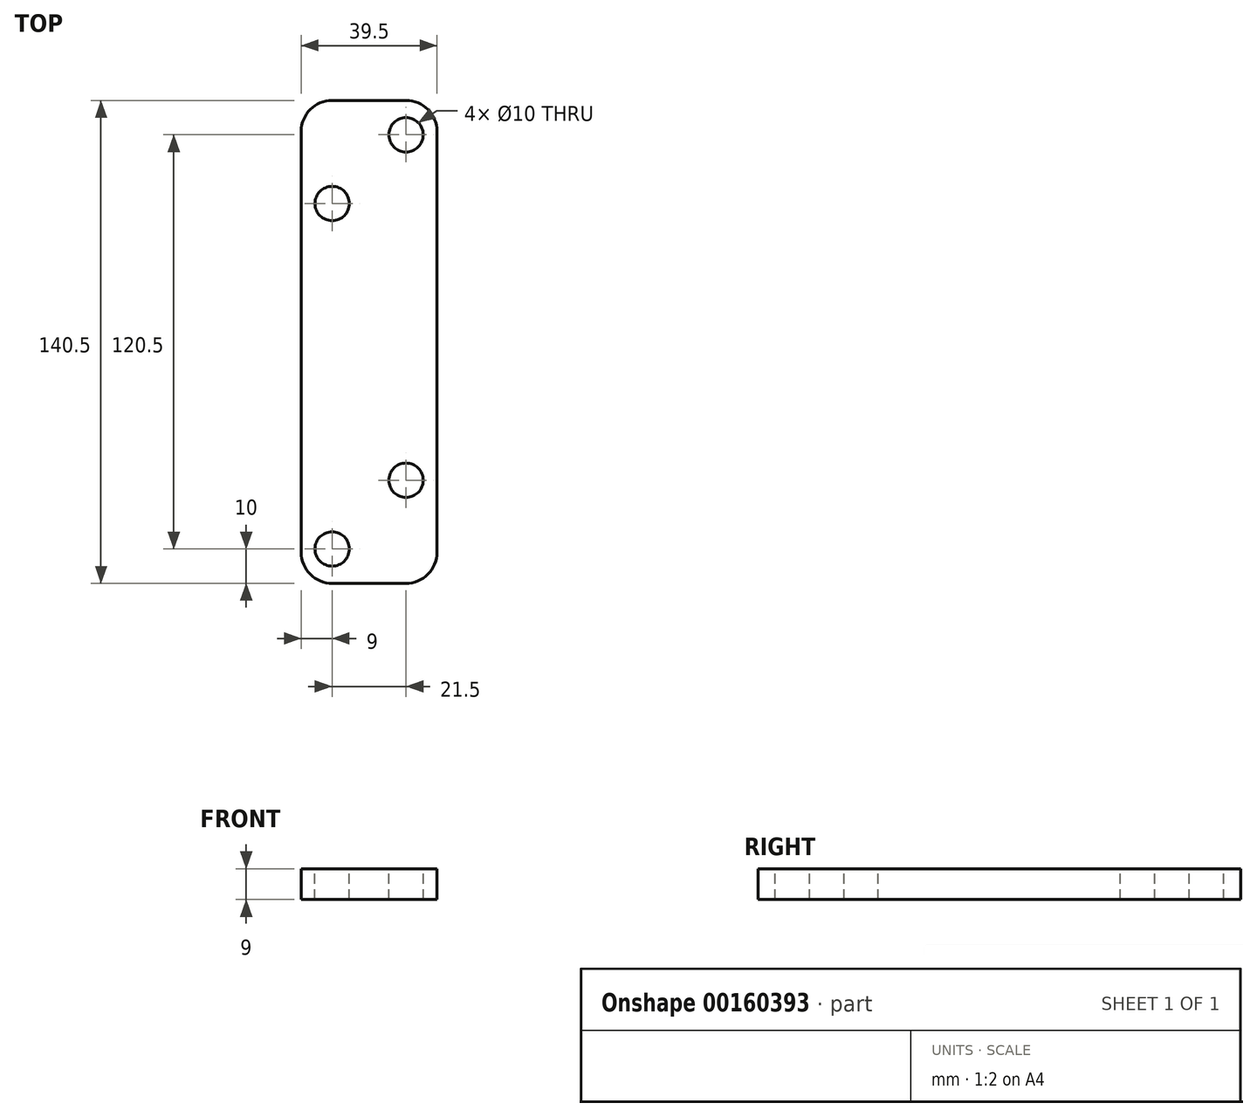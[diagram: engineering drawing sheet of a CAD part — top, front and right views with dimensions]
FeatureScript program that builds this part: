
annotation { "Feature Type Name" : "Feature", "Feature Type Description" : "" }
export const myFeature = defineFeature(function(context is Context, id is Id, definition is map)
    precondition{}
    {
        {
            var Q0;
            Q0=qCreatedBy(makeId("Top.planeOp"),FACE);
            var sketch = newSketch(context, id + "F0", { "sketchPlane" : qUnion([Q0])});
            skLineSegment(sketch, "E0.bottom", {"start": v(-10.75, 65.25) * mm, "end": v(10.75, 65.25) * mm, "construction": true});
            skLineSegment(sketch, "E0.top", {"start": v(-10.75, -65.25) * mm, "end": v(10.75, -65.25) * mm, "construction": true});
            skLineSegment(sketch, "E0.left", {"start": v(-14.75, 61.25) * mm, "end": v(-14.75, -61.25) * mm, "construction": true});
            skLineSegment(sketch, "E0.right", {"start": v(14.75, 61.25) * mm, "end": v(14.75, -61.25) * mm, "construction": true});
            skPoint(sketch, "E0.middle", {"position": v(0, 0) * mm});
            skPoint(sketch, "E1.visualSharp", {"position": v(-14.75, 65.25) * mm});
            skArc(sketch, "E1.filletArc", {"start": v(-10.75, 65.25) * mm, "mid": v(-13.58, 64.08) * mm, "end": v(-14.75, 61.25) * mm, "construction": true});
            skPoint(sketch, "E2.visualSharp", {"position": v(14.75, 65.25) * mm});
            skArc(sketch, "E2.filletArc", {"start": v(14.75, 61.25) * mm, "mid": v(13.58, 64.08) * mm, "end": v(10.75, 65.25) * mm, "construction": true});
            skPoint(sketch, "E3.visualSharp", {"position": v(14.75, -65.25) * mm});
            skArc(sketch, "E3.filletArc", {"start": v(10.75, -65.25) * mm, "mid": v(13.58, -64.08) * mm, "end": v(14.75, -61.25) * mm, "construction": true});
            skPoint(sketch, "E4.visualSharp", {"position": v(-14.75, -65.25) * mm});
            skArc(sketch, "E4.filletArc", {"start": v(-14.75, -61.25) * mm, "mid": v(-13.58, -64.08) * mm, "end": v(-10.75, -65.25) * mm, "construction": true});
            skArc(sketch, "E5.0", {"start": v(-10.75, 70.25) * mm, "mid": v(-17.11, 67.61) * mm, "end": v(-19.75, 61.25) * mm});
            skLineSegment(sketch, "E5.1", {"start": v(-10.75, 70.25) * mm, "end": v(10.75, 70.25) * mm});
            skLineSegment(sketch, "E5.2", {"start": v(-19.75, 61.25) * mm, "end": v(-19.75, -61.25) * mm});
            skArc(sketch, "E5.3", {"start": v(19.75, 61.25) * mm, "mid": v(17.11, 67.61) * mm, "end": v(10.75, 70.25) * mm});
            skArc(sketch, "E5.4", {"start": v(-19.75, -61.25) * mm, "mid": v(-17.11, -67.61) * mm, "end": v(-10.75, -70.25) * mm});
            skLineSegment(sketch, "E5.5", {"start": v(-10.75, -70.25) * mm, "end": v(10.75, -70.25) * mm});
            skArc(sketch, "E5.6", {"start": v(10.75, -70.25) * mm, "mid": v(17.11, -67.61) * mm, "end": v(19.75, -61.25) * mm});
            skLineSegment(sketch, "E5.7", {"start": v(19.75, 61.25) * mm, "end": v(19.75, -61.25) * mm});
            skSolve(sketch);
        }
        {
            var Q0;
            Q0=makeQuery(id+"F0.imprint","IMPRINT",FACE,{"disambiguationData":[TD([[makeQuery(id+"F0.imprint","IMPRINT",EDGE,{"derivedFrom":sQuery(id+"F0.wireOp",EDGE,"E5.0")}),1.0]])]});
            extrude(context, id + "F1", {"entities" : qUnion([Q0]), "depth" : 9 * mm});
        }
        {
            var Q0;
            Q0=makeQuery(id+"F1.opExtrude","CAP_FACE",FACE,{"disambiguationData":[OSD([sQuery(id+"F0.wireOp",EDGE,"E5.0"),sQuery(id+"F0.wireOp",EDGE,"E5.1"),sQuery(id+"F0.wireOp",EDGE,"E5.2"),sQuery(id+"F0.wireOp",EDGE,"E5.3"),sQuery(id+"F0.wireOp",EDGE,"E5.4"),sQuery(id+"F0.wireOp",EDGE,"E5.5"),sQuery(id+"F0.wireOp",EDGE,"E5.6"),sQuery(id+"F0.wireOp",EDGE,"E5.7")])],"isStart":false});
            var sketch = newSketch(context, id + "F2", { "sketchPlane" : qUnion([Q0])});
            skCircle(sketch, "E6", {"center": v(10.75, 60.25) * mm, "radius": 5 * mm});
            skCircle(sketch, "E7", {"center": v(-10.75, 40.25) * mm, "radius": 5 * mm});
            skCircle(sketch, "E8", {"center": v(10.75, -40.25) * mm, "radius": 5 * mm});
            skCircle(sketch, "E9", {"center": v(-10.75, -60.25) * mm, "radius": 5 * mm});
            skSolve(sketch);
        }
        {
            var Q0;
            Q0 = qSketchRegion(id + "F2", true);
            extrude(context, id + "F3", {"entities" : qUnion([Q0]), "operationType" : NewBodyOperationType.REMOVE, "endBound" : BoundingType.THROUGH_ALL, "oppositeDirection" : true, "depth" : 25 * mm});
        }
    });
